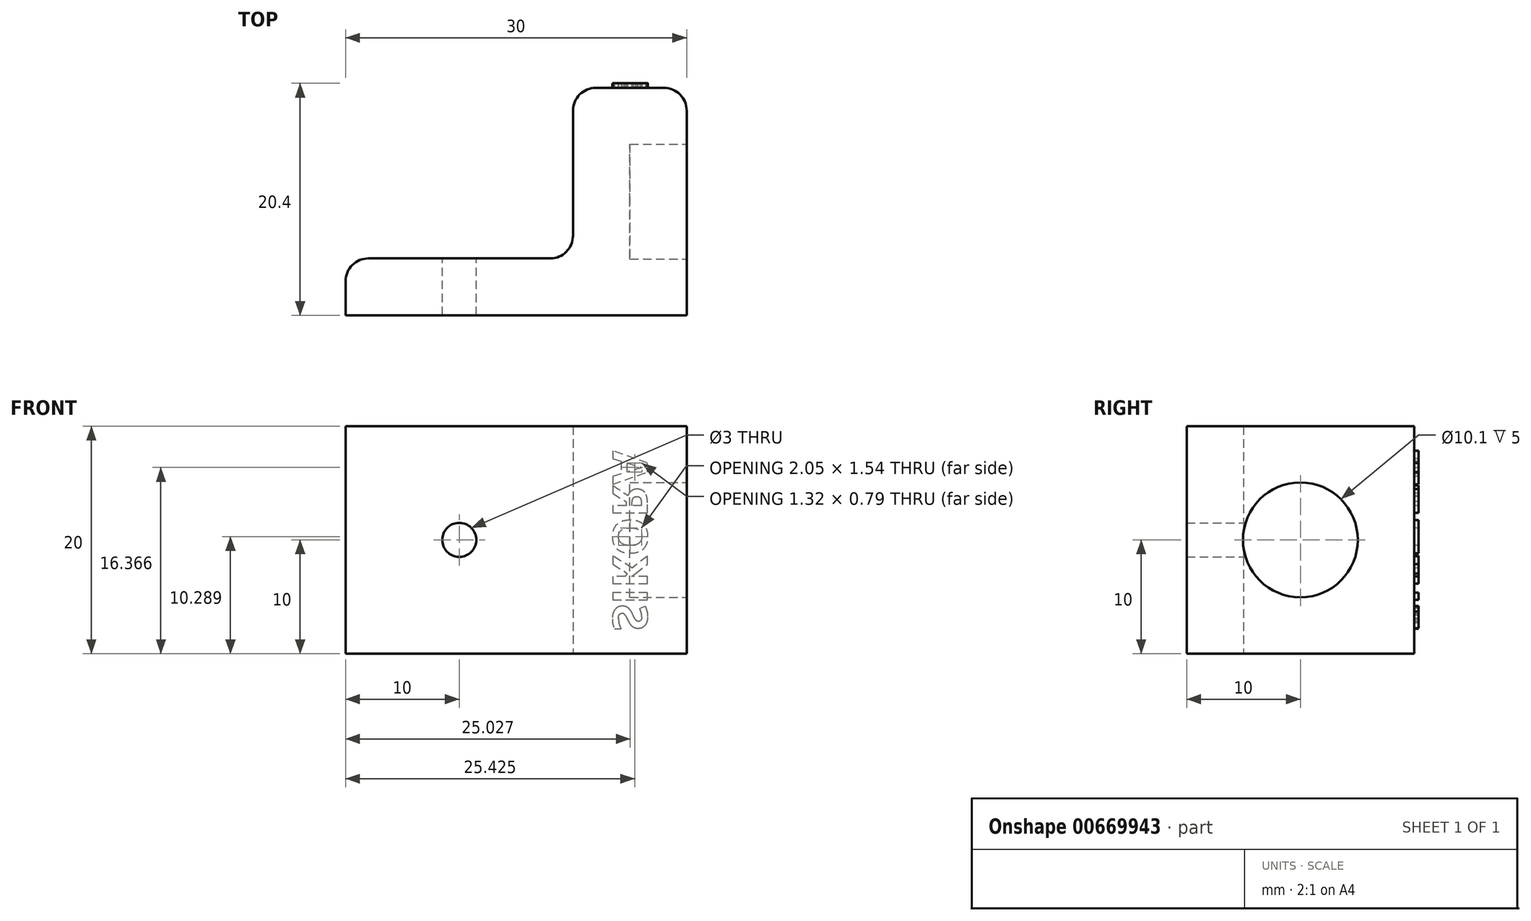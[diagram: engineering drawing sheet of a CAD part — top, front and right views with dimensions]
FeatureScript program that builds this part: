
annotation { "Feature Type Name" : "Feature", "Feature Type Description" : "" }
export const myFeature = defineFeature(function(context is Context, id is Id, definition is map)
    precondition{}
    {
        {
            var Q0;
            Q0=qCreatedBy(makeId("Top.planeOp"),FACE);
            var sketch = newSketch(context, id + "F0", { "sketchPlane" : qUnion([Q0])});
            skLineSegment(sketch, "E0", {"start": v(20, 0) * mm, "end": v(20, 15) * mm});
            skLineSegment(sketch, "E1.0", {"start": v(30, -5) * mm, "end": v(30, 15) * mm});
            skLineSegment(sketch, "E1.1", {"start": v(0, -5) * mm, "end": v(30, -5) * mm});
            skLineSegment(sketch, "E2", {"start": v(20, 15) * mm, "end": v(30, 15) * mm});
            skLineSegment(sketch, "E3", {"start": v(0, 0) * mm, "end": v(0, -5) * mm});
            skLineSegment(sketch, "E4", {"start": v(0, 0) * mm, "end": v(20, 0) * mm});
            skSolve(sketch);
        }
        {
            var Q0;
            Q0=makeQuery(id+"F0.imprint","IMPRINT",FACE,{"disambiguationData":[TD([[makeQuery(id+"F0.imprint","IMPRINT",EDGE,{"derivedFrom":sQuery(id+"F0.wireOp",EDGE,"E0")}),-1.0]])]});
            extrude(context, id + "F1", {"entities" : qUnion([Q0]), "depth" : 20 * mm, "offsetDistance" : 25 * mm});
        }
        {
            var Q0;
            Q0=makeQuery(id+"F1.opExtrude","SWEPT_FACE",FACE,{"disambiguationData":[OSD([sQuery(id+"F0.wireOp",EDGE,"E1.0")])]});
            var sketch = newSketch(context, id + "F2", { "sketchPlane" : qUnion([Q0])});
            skCircle(sketch, "E5", {"center": v(5, 10) * mm, "radius": 5.05 * mm});
            skPoint(sketch, "E5.centerSnap0", {"position": v(5, 20) * mm});
            skPoint(sketch, "E5.centerSnap1", {"position": v(15, 10) * mm});
            skSolve(sketch);
        }
        {
            var Q0;
            Q0=makeQuery(id+"F2.imprint","IMPRINT",FACE,{"disambiguationData":[TD([[makeQuery(id+"F2.imprint","IMPRINT",EDGE,{"derivedFrom":sQuery(id+"F2.wireOp",EDGE,"E5")}),1.0]])]});
            extrude(context, id + "F3", {"entities" : qUnion([Q0]), "operationType" : NewBodyOperationType.REMOVE, "oppositeDirection" : true, "depth" : 5 * mm, "offsetDistance" : 25 * mm});
        }
        {
            var Q0;
            Q0=makeQuery(id+"F1.opExtrude","SWEPT_FACE",FACE,{"disambiguationData":[OSD([sQuery(id+"F0.wireOp",EDGE,"E4")])]});
            var sketch = newSketch(context, id + "F4", { "sketchPlane" : qUnion([Q0])});
            skCircle(sketch, "E6", {"center": v(-10, 10) * mm, "radius": 1.5 * mm});
            skPoint(sketch, "E6.centerSnap0", {"position": v(0, 10) * mm});
            skPoint(sketch, "E6.centerSnap1", {"position": v(-10, 20) * mm});
            skSolve(sketch);
        }
        {
            var Q0;
            Q0=makeQuery(id+"F4.imprint","IMPRINT",FACE,{"disambiguationData":[TD([[makeQuery(id+"F4.imprint","IMPRINT",EDGE,{"derivedFrom":sQuery(id+"F4.wireOp",EDGE,"E6")}),1.0]])]});
            var Q1;
            Q1=sQuery(id+"F4.wireOp",EDGE,"E6");
            extrude(context, id + "F5", {"entities" : qUnion([Q0]), "operationType" : NewBodyOperationType.REMOVE, "surfaceEntities" : qUnion([Q1]), "oppositeDirection" : true, "depth" : 25 * mm, "offsetDistance" : 25 * mm});
        }
        {
            var Q0;
            Q0=makeQuery(id+"F1.opExtrude","SWEPT_EDGE",EDGE,{"disambiguationData":[OSD([sQuery(id+"F0.wireOp",EDGE,"E0"),sQuery(id+"F0.wireOp",EDGE,"E4")])]});
            var Q1;
            Q1=makeQuery(id+"F1.opExtrude","SWEPT_EDGE",EDGE,{"disambiguationData":[OSD([sQuery(id+"F0.wireOp",EDGE,"E3"),sQuery(id+"F0.wireOp",EDGE,"E4")])]});
            var Q2;
            Q2=makeQuery(id+"F1.opExtrude","SWEPT_EDGE",EDGE,{"disambiguationData":[OSD([sQuery(id+"F0.wireOp",EDGE,"E1.0"),sQuery(id+"F0.wireOp",EDGE,"E2")])]});
            var Q3;
            Q3=makeQuery(id+"F1.opExtrude","SWEPT_EDGE",EDGE,{"disambiguationData":[OSD([sQuery(id+"F0.wireOp",EDGE,"E0"),sQuery(id+"F0.wireOp",EDGE,"E2")])]});
            fillet(context, id + "F6", {"entities" : qUnion([Q0, Q1, Q2, Q3]), "radius" : 2 * mm, "tangentPropagation" : true, "allowEdgeOverflow" : false});
        }
        {
            var Q0;
            Q0=makeQuery(id+"F1.opExtrude","SWEPT_FACE",FACE,{"disambiguationData":[OSD([sQuery(id+"F0.wireOp",EDGE,"E2")])]});
            var sketch = newSketch(context, id + "F7", { "sketchPlane" : qUnion([Q0])});
            skText(sketch, "E7", { "text": "SIKORA", "fontName": "OpenSans-Bold.ttf"});
            const initialGuessF7  = {"E7": [-0.0235, 0.002, 0, 1, 0.00307]};
            skSetInitialGuess(sketch, initialGuessF7);
            skSolve(sketch);
        }
        {
            var Q0;
            Q0 = qSketchRegion(id + "F7", true);
            extrude(context, id + "F8", {"entities" : qUnion([Q0]), "depth" : .4 * mm, "offsetDistance" : 25 * mm});
        }
    });
